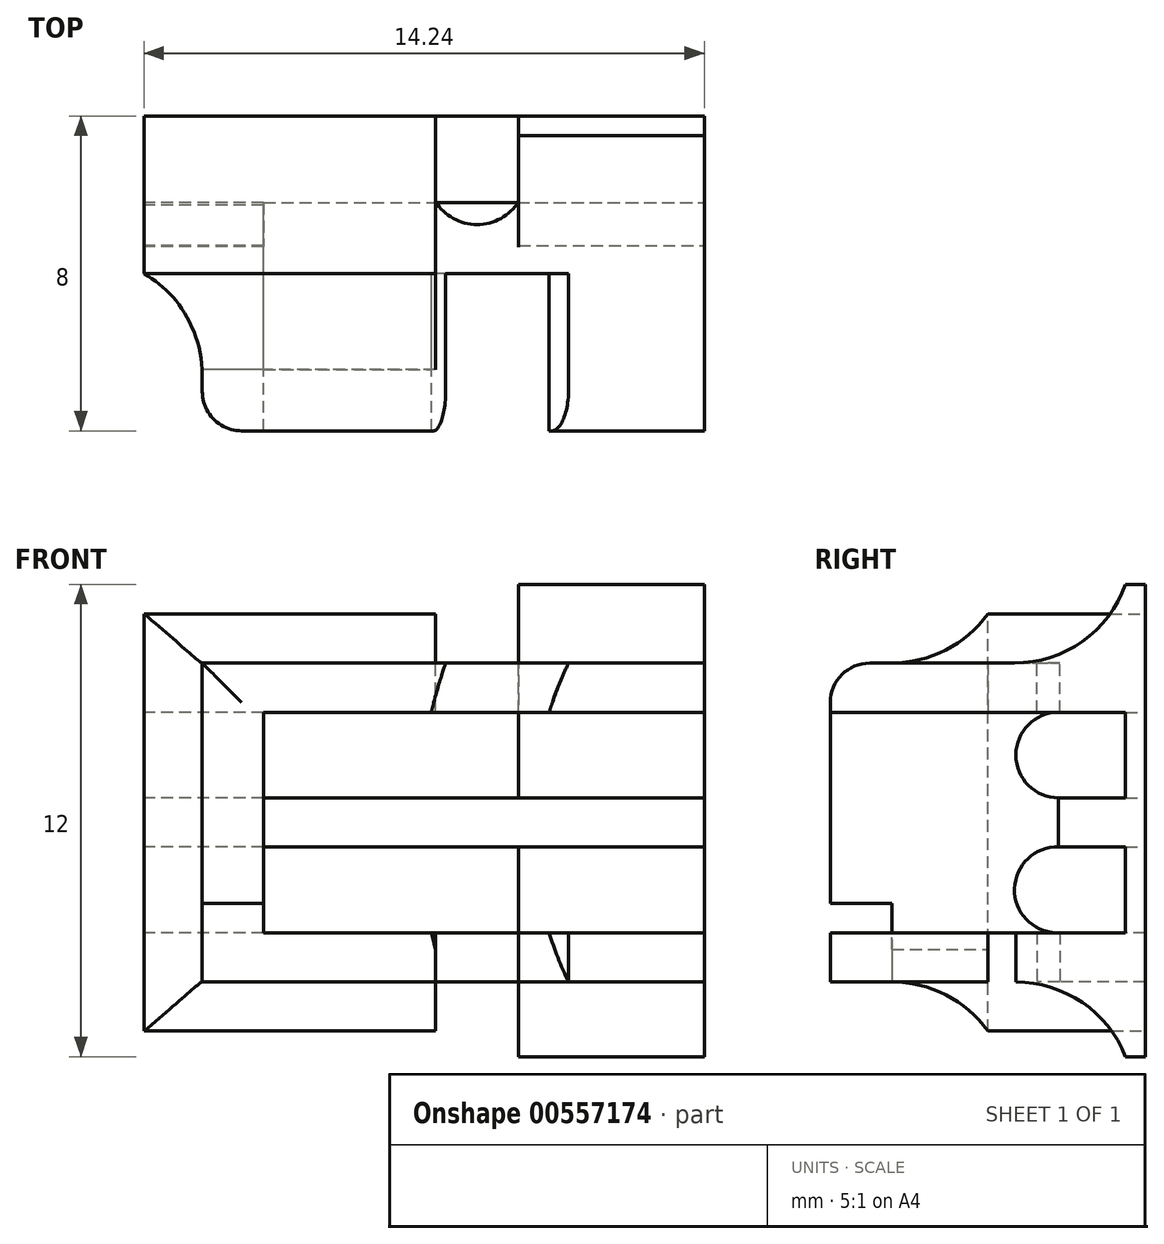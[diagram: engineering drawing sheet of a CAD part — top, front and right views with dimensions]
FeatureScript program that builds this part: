
annotation { "Feature Type Name" : "Feature", "Feature Type Description" : "" }
export const myFeature = defineFeature(function(context is Context, id is Id, definition is map)
    precondition{}
    {
        {
            var Q0;
            Q0=qCreatedBy(makeId("Front.planeOp"),FACE);
            var sketch = newSketch(context, id + "F0", { "sketchPlane" : qUnion([Q0])});
            skLineSegment(sketch, "E0.bottom", {"start": v(-5.6, 2.8) * mm, "end": v(-1.74, 2.8) * mm, "construction": true});
            skLineSegment(sketch, "E0.top", {"start": v(-5.6, -2.8) * mm, "end": v(-1.74, -2.8) * mm, "construction": true});
            skLineSegment(sketch, "E0.left", {"start": v(-5.6, 2.8) * mm, "end": v(-5.6, -2.8) * mm, "construction": true});
            skLineSegment(sketch, "E0.right", {"start": v(5.6, 2.8) * mm, "end": v(5.6, -2.8) * mm, "construction": true});
            skPoint(sketch, "E0.middle", {"position": v(0, 0) * mm});
            skLineSegment(sketch, "E1.bottom", {"start": v(-5.6, 0.62) * mm, "end": v(-1.23, 0.62) * mm});
            skLineSegment(sketch, "E1.top", {"start": v(-5.6, -0.62) * mm, "end": v(-1.23, -0.62) * mm});
            skLineSegment(sketch, "E1.left", {"start": v(-5.6, 0.62) * mm, "end": v(-5.6, -0.62) * mm});
            skLineSegment(sketch, "E1.right", {"start": v(5.6, 0.62) * mm, "end": v(5.6, -0.62) * mm});
            skLineSegment(sketch, "E2.bottom", {"start": v(-5.6, 4.05) * mm, "end": v(-1.23, 4.05) * mm});
            skLineSegment(sketch, "E2.top", {"start": v(-5.6, 2.8) * mm, "end": v(-1.74, 2.8) * mm});
            skLineSegment(sketch, "E2.left", {"start": v(-5.6, 4.05) * mm, "end": v(-5.6, 2.8) * mm});
            skLineSegment(sketch, "E2.right", {"start": v(5.6, 4.05) * mm, "end": v(5.6, 2.8) * mm});
            skLineSegment(sketch, "E3.bottom", {"start": v(5.6, -4.05) * mm, "end": v(0.88, -4.05) * mm});
            skLineSegment(sketch, "E3.top", {"start": v(5.6, -2.8) * mm, "end": v(1.23, -2.8) * mm});
            skLineSegment(sketch, "E3.left", {"start": v(5.6, -4.05) * mm, "end": v(5.6, -2.8) * mm});
            skLineSegment(sketch, "E3.right", {"start": v(-5.6, -4.05) * mm, "end": v(-5.6, -2.8) * mm});
            skLineSegment(sketch, "E4", {"start": v(1.23, 2.8) * mm, "end": v(1.23, 0.63) * mm, "construction": true});
            skLineSegment(sketch, "E5", {"start": v(-1.23, 2.8) * mm, "end": v(-1.23, 0.63) * mm, "construction": true});
            skLineSegment(sketch, "E6.bottom", {"start": v(-5.6, 4.05) * mm, "end": v(-7.16, 4.05) * mm});
            skLineSegment(sketch, "E6.top", {"start": v(-5.6, -4.05) * mm, "end": v(-7.16, -4.05) * mm});
            skLineSegment(sketch, "E6.left", {"start": v(-5.6, 4.05) * mm, "end": v(-5.6, -4.05) * mm});
            skLineSegment(sketch, "E6.right", {"start": v(-7.16, 4.05) * mm, "end": v(-7.16, -4.05) * mm});
            skLineSegment(sketch, "E7", {"start": v(-1.23, 4.05) * mm, "end": v(-1.23, 5.3) * mm});
            skLineSegment(sketch, "E8", {"start": v(-1.23, 5.3) * mm, "end": v(-8.64, 5.3) * mm});
            skLineSegment(sketch, "E9", {"start": v(-1.23, -4.05) * mm, "end": v(-1.23, -5.3) * mm});
            skLineSegment(sketch, "E10", {"start": v(-1.23, -5.3) * mm, "end": v(-8.64, -5.3) * mm});
            skLineSegment(sketch, "E11", {"start": v(-8.64, -5.3) * mm, "end": v(-8.64, 5.3) * mm});
            skLineSegment(sketch, "E12.trimOffspring", {"start": v(1.64, 0.62) * mm, "end": v(5.6, 0.62) * mm});
            skLineSegment(sketch, "E13.trimOffspring", {"start": v(1.64, -0.62) * mm, "end": v(5.6, -0.62) * mm});
            skLineSegment(sketch, "E14.trimOffspring", {"start": v(1.23, -2.8) * mm, "end": v(5.6, -2.8) * mm, "construction": true});
            skLineSegment(sketch, "E15.trimOffspring", {"start": v(-1.23, -4.05) * mm, "end": v(-5.6, -4.05) * mm});
            skLineSegment(sketch, "E16.trimOffspring", {"start": v(1.23, 2.8) * mm, "end": v(5.6, 2.8) * mm, "construction": true});
            skLineSegment(sketch, "E17.trimOffspring", {"start": v(1.23, 2.8) * mm, "end": v(5.6, 2.8) * mm});
            skLineSegment(sketch, "E18.trimOffspring", {"start": v(0.88, 4.05) * mm, "end": v(5.6, 4.05) * mm});
            skLineSegment(sketch, "E19.trimOffspring", {"start": v(-1.23, -2.8) * mm, "end": v(-5.6, -2.8) * mm});
            skLineSegment(sketch, "E20", {"start": v(-1.74, 2.8) * mm, "end": v(1.3, 2.8) * mm});
            skLineSegment(sketch, "E21", {"start": v(-2.33, 4.05) * mm, "end": v(0.88, 4.05) * mm});
            skLineSegment(sketch, "E22", {"start": v(-2.33, -4.05) * mm, "end": v(0.88, -4.05) * mm});
            skLineSegment(sketch, "E23", {"start": v(-1.74, -2.8) * mm, "end": v(1.23, -2.8) * mm});
            skLineSegment(sketch, "E24", {"start": v(-1.23, 0.62) * mm, "end": v(1.64, 0.62) * mm});
            skLineSegment(sketch, "E25", {"start": v(-1.23, -0.62) * mm, "end": v(1.64, -0.62) * mm});
            skLineSegment(sketch, "E26.trimOffspring", {"start": v(-1.23, -0.62) * mm, "end": v(-1.23, -2.8) * mm, "construction": true});
            skLineSegment(sketch, "E27.trimOffspring", {"start": v(1.23, -0.63) * mm, "end": v(1.23, -2.8) * mm, "construction": true});
            skArc(sketch, "E28", {"start": v(2.15, 4.05) * mm, "mid": v(1.88, 3.43) * mm, "end": v(1.66, 2.8) * mm});
            skArc(sketch, "E29.0", {"start": v(-0.97, 4.05) * mm, "mid": v(-1.17, 3.43) * mm, "end": v(-1.34, 2.8) * mm});
            skArc(sketch, "E30.trimOffspring", {"start": v(-1.64, 0.63) * mm, "mid": v(-1.66, 0) * mm, "end": v(-1.64, -0.62) * mm});
            skArc(sketch, "E31.trimOffspring", {"start": v(-1.34, -2.8) * mm, "mid": v(-1.17, -3.43) * mm, "end": v(-0.97, -4.05) * mm});
            skArc(sketch, "E32.trimOffspring", {"start": v(1.25, 0.62) * mm, "mid": v(1.23, 0) * mm, "end": v(1.25, -0.63) * mm});
            skArc(sketch, "E33.trimOffspring", {"start": v(1.66, -2.8) * mm, "mid": v(1.88, -3.43) * mm, "end": v(2.15, -4.05) * mm});
            skSolve(sketch);
        }
        {
            var Q0;
            {var subQ0=sQuery(id+"F0.wireOp",EDGE,"E1.bottom");Q0=makeQuery(id+"F0.imprint","IMPRINT",FACE,{"disambiguationData":[TD([[makeQuery(id+"F0.imprint","IMPRINT",EDGE,{"derivedFrom":subQ0}),-1.0]])]});}
            var Q1;
            {var subQ7=sQuery(id+"F0.wireOp",EDGE,"E30.trimOffspring");Q1=makeQuery(id+"F0.imprint","IMPRINT",FACE,{"disambiguationData":[TD([[makeQuery(id+"F0.imprint","IMPRINT",EDGE,{"derivedFrom":subQ7}),1.0]])]});}
            var Q2;
            Q2=makeQuery(id+"F0.imprint","IMPRINT",FACE,{"disambiguationData":[TD([[makeQuery(id+"F0.imprint","IMPRINT",EDGE,{"derivedFrom":sQuery(id+"F0.wireOp",EDGE,"E1.right")}),-1.0]])]});
            extrude(context, id + "F1", {"entities" : qUnion([Q0, Q1, Q2]), "depth" : 2.2 * mm, "offsetDistance" : 25 * mm});
        }
        {
            var Q0;
            {var subQ0=sQuery(id+"F0.wireOp",EDGE,"E3.left");Q0=makeQuery(id+"F0.imprint","IMPRINT",FACE,{"disambiguationData":[TD([[makeQuery(id+"F0.imprint","IMPRINT",EDGE,{"derivedFrom":subQ0}),1.0]])]});}
            var Q1;
            {var subQ3=sQuery(id+"F0.wireOp",EDGE,"E31.trimOffspring");Q1=makeQuery(id+"F0.imprint","IMPRINT",FACE,{"disambiguationData":[TD([[makeQuery(id+"F0.imprint","IMPRINT",EDGE,{"derivedFrom":subQ3}),1.0]])]});}
            var Q2;
            {var subQ1=sQuery(id+"F0.wireOp",EDGE,"E15.trimOffspring");Q2=makeQuery(id+"F0.imprint","IMPRINT",FACE,{"disambiguationData":[TD([[makeQuery(id+"F0.imprint","IMPRINT",EDGE,{"derivedFrom":subQ1}),-1.0]])]});}
            var Q3;
            {var subQ1=sQuery(id+"F0.wireOp",EDGE,"E2.bottom");Q3=makeQuery(id+"F0.imprint","IMPRINT",FACE,{"disambiguationData":[TD([[makeQuery(id+"F0.imprint","IMPRINT",EDGE,{"derivedFrom":subQ1}),1.0]])]});}
            var Q4;
            {var subQ3=sQuery(id+"F0.wireOp",EDGE,"E6.bottom");Q4=makeQuery(id+"F0.imprint","IMPRINT",FACE,{"disambiguationData":[TD([[makeQuery(id+"F0.imprint","IMPRINT",EDGE,{"derivedFrom":subQ3}),1.0]])]});}
            var Q5;
            {var subQ4=sQuery(id+"F0.wireOp",EDGE,"E2.bottom");Q5=makeQuery(id+"F0.imprint","IMPRINT",FACE,{"disambiguationData":[TD([[makeQuery(id+"F0.imprint","IMPRINT",EDGE,{"derivedFrom":subQ4}),-1.0]])]});}
            var Q6;
            {var subQ7=sQuery(id+"F0.wireOp",EDGE,"E28");Q6=makeQuery(id+"F0.imprint","IMPRINT",FACE,{"disambiguationData":[TD([[makeQuery(id+"F0.imprint","IMPRINT",EDGE,{"derivedFrom":subQ7}),-1.0]])]});}
            var Q7;
            {var subQ0=sQuery(id+"F0.wireOp",EDGE,"E2.right");Q7=makeQuery(id+"F0.imprint","IMPRINT",FACE,{"disambiguationData":[TD([[makeQuery(id+"F0.imprint","IMPRINT",EDGE,{"derivedFrom":subQ0}),-1.0]])]});}
            extrude(context, id + "F2", {"entities" : qUnion([Q0, Q1, Q2, Q3, Q4, Q5, Q6, Q7]), "operationType" : NewBodyOperationType.ADD, "depth" : 4 * mm, "offsetDistance" : 25 * mm});
        }
        {
            var Q0;
            {var subQ0=sQuery(id+"F0.wireOp",EDGE,"E2.right");Q0=makeQuery(id+"F0.imprint","IMPRINT",FACE,{"disambiguationData":[TD([[makeQuery(id+"F0.imprint","IMPRINT",EDGE,{"derivedFrom":subQ0}),-1.0]])]});}
            var Q1;
            {var subQ4=sQuery(id+"F0.wireOp",EDGE,"E2.bottom");Q1=makeQuery(id+"F0.imprint","IMPRINT",FACE,{"disambiguationData":[TD([[makeQuery(id+"F0.imprint","IMPRINT",EDGE,{"derivedFrom":subQ4}),-1.0]])]});}
            var Q2;
            {var subQ3=sQuery(id+"F0.wireOp",EDGE,"E6.bottom");Q2=makeQuery(id+"F0.imprint","IMPRINT",FACE,{"disambiguationData":[TD([[makeQuery(id+"F0.imprint","IMPRINT",EDGE,{"derivedFrom":subQ3}),1.0]])]});}
            var Q3;
            {var subQ1=sQuery(id+"F0.wireOp",EDGE,"E15.trimOffspring");Q3=makeQuery(id+"F0.imprint","IMPRINT",FACE,{"disambiguationData":[TD([[makeQuery(id+"F0.imprint","IMPRINT",EDGE,{"derivedFrom":subQ1}),-1.0]])]});}
            var Q4;
            {var subQ0=sQuery(id+"F0.wireOp",EDGE,"E3.left");Q4=makeQuery(id+"F0.imprint","IMPRINT",FACE,{"disambiguationData":[TD([[makeQuery(id+"F0.imprint","IMPRINT",EDGE,{"derivedFrom":subQ0}),1.0]])]});}
            extrude(context, id + "F3", {"entities" : qUnion([Q0, Q1, Q2, Q3, Q4]), "operationType" : NewBodyOperationType.ADD, "depth" : 8 * mm, "offsetDistance" : 25 * mm});
        }
        {
            var Q0;
            Q0=makeQuery(id+"F2.opExtrude","SWEPT_FACE",FACE,{"disambiguationData":[OSD([sQuery(id+"F0.wireOp",EDGE,"E11")])]});
            var sketch = newSketch(context, id + "F4", { "sketchPlane" : qUnion([Q0])});
            skLineSegment(sketch, "E34.0", {"start": v(8, 2.8) * mm, "end": v(0, 2.8) * mm});
            skLineSegment(sketch, "E34.1", {"start": v(2.2, 0.62) * mm, "end": v(0, 0.62) * mm});
            skLineSegment(sketch, "E34.2", {"start": v(2.2, 0.62) * mm, "end": v(2.2, -0.62) * mm});
            skLineSegment(sketch, "E34.3", {"start": v(2.2, -0.62) * mm, "end": v(0, -0.62) * mm});
            skLineSegment(sketch, "E34.4", {"start": v(8, -2.8) * mm, "end": v(0, -2.8) * mm});
            skLineSegment(sketch, "E35", {"start": v(2.2, 2.8) * mm, "end": v(2.2, -2.8) * mm, "construction": true});
            skArc(sketch, "E36", {"start": v(2.2, 0.62) * mm, "mid": v(3.29, 1.71) * mm, "end": v(2.2, 2.8) * mm});
            skArc(sketch, "E37", {"start": v(2.2, -2.8) * mm, "mid": v(3.32, -1.71) * mm, "end": v(2.2, -0.63) * mm});
            skSolve(sketch);
        }
        {
            var Q0;
            {var subQ0=sQuery(id+"F0.wireOp",EDGE,"E18.trimOffspring");Q0=makeQuery(id+"F3.boolean.opBoolean","MERGE",FACE,{"derivedFrom":[makeQuery(id+"F2.opExtrude","SWEPT_FACE",FACE,{"disambiguationData":[OSD([subQ0,sQuery(id+"F0.wireOp",EDGE,"E21")])]}),makeQuery(id+"F3.opExtrude","SWEPT_FACE",FACE,{"disambiguationData":[OSD([subQ0])]})]});}
            var sketch = newSketch(context, id + "F5", { "sketchPlane" : qUnion([Q0])});
            skLineSegment(sketch, "E38.bottom", {"start": v(5.6, 0) * mm, "end": v(0.88, 0) * mm});
            skLineSegment(sketch, "E38.top", {"start": v(5.6, -0.5) * mm, "end": v(0.88, -0.5) * mm});
            skLineSegment(sketch, "E38.left", {"start": v(5.6, 0) * mm, "end": v(5.6, -0.5) * mm});
            skLineSegment(sketch, "E38.right", {"start": v(0.88, 0) * mm, "end": v(0.88, -0.5) * mm});
            skSolve(sketch);
        }
        {
            var Q0;
            Q0=makeQuery(id+"F5.imprint","IMPRINT",FACE,{"disambiguationData":[TD([[makeQuery(id+"F5.imprint","IMPRINT",EDGE,{"derivedFrom":sQuery(id+"F5.wireOp",EDGE,"E38.bottom")}),-1.0]])]});
            extrude(context, id + "F6", {"entities" : qUnion([Q0]), "operationType" : NewBodyOperationType.ADD, "depth" : 2 * mm, "offsetDistance" : 25 * mm, "hasSecondDirection" : true, "secondDirectionOppositeDirection" : true, "secondDirectionDepth" : 10 * mm});
        }
        {
            var Q0;
            {var subQ4=sQuery(id+"F4.wireOp",EDGE,"E34.1");Q0=makeQuery(id+"F4.imprint","IMPRINT",FACE,{"disambiguationData":[TD([[makeQuery(id+"F4.imprint","IMPRINT",EDGE,{"derivedFrom":subQ4}),-1.0]])]});}
            var Q1;
            {var subQ1=sQuery(id+"F4.wireOp",EDGE,"E34.3");Q1=makeQuery(id+"F4.imprint","IMPRINT",FACE,{"disambiguationData":[TD([[makeQuery(id+"F4.imprint","IMPRINT",EDGE,{"derivedFrom":subQ1}),1.0]])]});}
            extrude(context, id + "F7", {"entities" : qUnion([Q0, Q1]), "operationType" : NewBodyOperationType.REMOVE, "oppositeDirection" : true, "depth" : 4 * mm, "offsetDistance" : 25 * mm});
        }
        {
            var Q0;
            {var subQ0=sQuery(id+"F0.wireOp",EDGE,"E21");Q0=makeQuery(id+"F3.boolean.opBoolean","INTERSECT",EDGE,{"derivedFrom":[makeQuery(id+"F2.opExtrude","CAP_FACE",FACE,{"disambiguationData":[OSD([sQuery(id+"F0.wireOp",EDGE,"E2.top"),sQuery(id+"F0.wireOp",EDGE,"E2.right"),sQuery(id+"F0.wireOp",EDGE,"E3.bottom"),sQuery(id+"F0.wireOp",EDGE,"E3.top"),sQuery(id+"F0.wireOp",EDGE,"E3.left"),sQuery(id+"F0.wireOp",EDGE,"E6.left"),sQuery(id+"F0.wireOp",EDGE,"E7"),sQuery(id+"F0.wireOp",EDGE,"E8"),sQuery(id+"F0.wireOp",EDGE,"E9"),sQuery(id+"F0.wireOp",EDGE,"E10"),sQuery(id+"F0.wireOp",EDGE,"E11"),sQuery(id+"F0.wireOp",EDGE,"E17.trimOffspring"),sQuery(id+"F0.wireOp",EDGE,"E18.trimOffspring"),sQuery(id+"F0.wireOp",EDGE,"E19.trimOffspring"),sQuery(id+"F0.wireOp",EDGE,"E20"),subQ0,sQuery(id+"F0.wireOp",EDGE,"E22"),sQuery(id+"F0.wireOp",EDGE,"E23")])],"isStart":false}),makeQuery(id+"F3.opExtrude","SWEPT_FACE",FACE,{"disambiguationData":[OSD([sQuery(id+"F0.wireOp",EDGE,"E2.bottom"),sQuery(id+"F0.wireOp",EDGE,"E6.bottom"),subQ0])]})]});}
            var Q1;
            Q1=makeQuery(id+"F3.boolean.opBoolean","INTERSECT",EDGE,{"derivedFrom":[makeQuery(id+"F2.opExtrude","CAP_FACE",FACE,{"disambiguationData":[OSD([sQuery(id+"F0.wireOp",EDGE,"E2.top"),sQuery(id+"F0.wireOp",EDGE,"E2.right"),sQuery(id+"F0.wireOp",EDGE,"E3.bottom"),sQuery(id+"F0.wireOp",EDGE,"E3.top"),sQuery(id+"F0.wireOp",EDGE,"E3.left"),sQuery(id+"F0.wireOp",EDGE,"E6.left"),sQuery(id+"F0.wireOp",EDGE,"E7"),sQuery(id+"F0.wireOp",EDGE,"E8"),sQuery(id+"F0.wireOp",EDGE,"E9"),sQuery(id+"F0.wireOp",EDGE,"E10"),sQuery(id+"F0.wireOp",EDGE,"E11"),sQuery(id+"F0.wireOp",EDGE,"E17.trimOffspring"),sQuery(id+"F0.wireOp",EDGE,"E18.trimOffspring"),sQuery(id+"F0.wireOp",EDGE,"E19.trimOffspring"),sQuery(id+"F0.wireOp",EDGE,"E20"),sQuery(id+"F0.wireOp",EDGE,"E21"),sQuery(id+"F0.wireOp",EDGE,"E22"),sQuery(id+"F0.wireOp",EDGE,"E23")])],"isStart":false}),makeQuery(id+"F3.opExtrude","SWEPT_FACE",FACE,{"disambiguationData":[OSD([sQuery(id+"F0.wireOp",EDGE,"E6.right")])]})]});
            var Q2;
            {var subQ0=sQuery(id+"F0.wireOp",EDGE,"E22");Q2=makeQuery(id+"F3.boolean.opBoolean","INTERSECT",EDGE,{"derivedFrom":[makeQuery(id+"F2.opExtrude","CAP_FACE",FACE,{"disambiguationData":[OSD([sQuery(id+"F0.wireOp",EDGE,"E2.top"),sQuery(id+"F0.wireOp",EDGE,"E2.right"),sQuery(id+"F0.wireOp",EDGE,"E3.bottom"),sQuery(id+"F0.wireOp",EDGE,"E3.top"),sQuery(id+"F0.wireOp",EDGE,"E3.left"),sQuery(id+"F0.wireOp",EDGE,"E6.left"),sQuery(id+"F0.wireOp",EDGE,"E7"),sQuery(id+"F0.wireOp",EDGE,"E8"),sQuery(id+"F0.wireOp",EDGE,"E9"),sQuery(id+"F0.wireOp",EDGE,"E10"),sQuery(id+"F0.wireOp",EDGE,"E11"),sQuery(id+"F0.wireOp",EDGE,"E17.trimOffspring"),sQuery(id+"F0.wireOp",EDGE,"E18.trimOffspring"),sQuery(id+"F0.wireOp",EDGE,"E19.trimOffspring"),sQuery(id+"F0.wireOp",EDGE,"E20"),sQuery(id+"F0.wireOp",EDGE,"E21"),subQ0,sQuery(id+"F0.wireOp",EDGE,"E23")])],"isStart":false}),makeQuery(id+"F3.opExtrude","SWEPT_FACE",FACE,{"disambiguationData":[OSD([sQuery(id+"F0.wireOp",EDGE,"E6.top"),sQuery(id+"F0.wireOp",EDGE,"E15.trimOffspring"),subQ0])]})]});}
            var Q3;
            {var subQ0=sQuery(id+"F0.wireOp",EDGE,"E22");var subQ1=sQuery(id+"F0.wireOp",EDGE,"E3.bottom");Q3=makeQuery(id+"F6.boolean.opBoolean","INTERSECT",EDGE,{"derivedFrom":[makeQuery(id+"F3.boolean.opBoolean","MERGE",FACE,{"derivedFrom":[makeQuery(id+"F2.opExtrude","SWEPT_FACE",FACE,{"disambiguationData":[OSD([subQ1,subQ0])]}),makeQuery(id+"F3.opExtrude","SWEPT_FACE",FACE,{"disambiguationData":[OSD([subQ1])]}),makeQuery(id+"F3.opExtrude","SWEPT_FACE",FACE,{"disambiguationData":[OSD([sQuery(id+"F0.wireOp",EDGE,"E6.top"),sQuery(id+"F0.wireOp",EDGE,"E15.trimOffspring"),subQ0])]})]}),makeQuery(id+"F6.opExtrude","SWEPT_FACE",FACE,{"disambiguationData":[OSD([sQuery(id+"F5.wireOp",EDGE,"E38.top")])]})]});}
            var Q4;
            {var subQ0=sQuery(id+"F0.wireOp",EDGE,"E18.trimOffspring");var subQ1=sQuery(id+"F0.wireOp",EDGE,"E21");Q4=makeQuery(id+"F6.boolean.opBoolean","INTERSECT",EDGE,{"derivedFrom":[makeQuery(id+"F3.boolean.opBoolean","MERGE",FACE,{"derivedFrom":[makeQuery(id+"F2.opExtrude","SWEPT_FACE",FACE,{"disambiguationData":[OSD([subQ0,subQ1])]}),makeQuery(id+"F3.opExtrude","SWEPT_FACE",FACE,{"disambiguationData":[OSD([sQuery(id+"F0.wireOp",EDGE,"E2.bottom"),sQuery(id+"F0.wireOp",EDGE,"E6.bottom"),subQ1])]}),makeQuery(id+"F3.opExtrude","SWEPT_FACE",FACE,{"disambiguationData":[OSD([subQ0])]})]}),makeQuery(id+"F6.opExtrude","SWEPT_FACE",FACE,{"disambiguationData":[OSD([sQuery(id+"F5.wireOp",EDGE,"E38.top")])]})]});}
            fillet(context, id + "F8", {"entities" : qUnion([Q0, Q1, Q2, Q3, Q4]), "radius" : 3 * mm, "tangentPropagation" : true, "allowEdgeOverflow" : false});
        }
        {
            var Q0;
            {var subQ0=sQuery(id+"F0.wireOp",EDGE,"E18.trimOffspring");var subQ1=sQuery(id+"F0.wireOp",EDGE,"E21");Q0=makeQuery(id+"F3.boolean.opBoolean","MERGE",FACE,{"derivedFrom":[makeQuery(id+"F2.opExtrude","SWEPT_FACE",FACE,{"disambiguationData":[OSD([subQ0,subQ1])]}),makeQuery(id+"F3.opExtrude","SWEPT_FACE",FACE,{"disambiguationData":[OSD([sQuery(id+"F0.wireOp",EDGE,"E2.bottom"),sQuery(id+"F0.wireOp",EDGE,"E6.bottom"),subQ1])]}),makeQuery(id+"F3.opExtrude","SWEPT_FACE",FACE,{"disambiguationData":[OSD([subQ0])]})]});}
            var sketch = newSketch(context, id + "F9", { "sketchPlane" : qUnion([Q0])});
            skLineSegment(sketch, "E39", {"start": v(0.88, -2.17) * mm, "end": v(-1.23, -2.17) * mm, "construction": true});
            skArc(sketch, "E40", {"start": v(-1.23, -2.17) * mm, "mid": v(-0.18, -2.76) * mm, "end": v(0.88, -2.17) * mm});
            skSolve(sketch);
        }
        {
            var Q0;
            {var subQ0=sQuery(id+"F9.wireOp",EDGE,"E40");Q0=makeQuery(id+"F9.imprint","IMPRINT",FACE,{"disambiguationData":[TD([[makeQuery(id+"F9.imprint","IMPRINT",EDGE,{"derivedFrom":subQ0}),1.0]])]});}
            extrude(context, id + "F10", {"entities" : qUnion([Q0]), "operationType" : NewBodyOperationType.REMOVE, "oppositeDirection" : true, "depth" : 1.5 * mm, "offsetDistance" : 25 * mm});
        }
        {
            var Q0;
            {var subQ0=sQuery(id+"F0.wireOp",EDGE,"E22");var subQ1=sQuery(id+"F0.wireOp",EDGE,"E3.bottom");Q0=makeQuery(id+"F3.boolean.opBoolean","MERGE",FACE,{"derivedFrom":[makeQuery(id+"F2.opExtrude","SWEPT_FACE",FACE,{"disambiguationData":[OSD([subQ1,subQ0])]}),makeQuery(id+"F3.opExtrude","SWEPT_FACE",FACE,{"disambiguationData":[OSD([subQ1])]}),makeQuery(id+"F3.opExtrude","SWEPT_FACE",FACE,{"disambiguationData":[OSD([sQuery(id+"F0.wireOp",EDGE,"E6.top"),sQuery(id+"F0.wireOp",EDGE,"E15.trimOffspring"),subQ0])]})]});}
            var sketch = newSketch(context, id + "F11", { "sketchPlane" : qUnion([Q0])});
            skArc(sketch, "E41.0", {"start": v(-1.23, 2.17) * mm, "mid": v(-0.18, 2.76) * mm, "end": v(0.88, 2.17) * mm});
            skLineSegment(sketch, "E41.1", {"start": v(0.88, 0.5) * mm, "end": v(0.88, 3.3) * mm});
            skLineSegment(sketch, "E41.2", {"start": v(0.88, 0) * mm, "end": v(0.88, 0.5) * mm});
            skLineSegment(sketch, "E41.3", {"start": v(-1.23, 4) * mm, "end": v(-1.23, 0) * mm});
            skSolve(sketch);
        }
        {
            var Q0;
            {var subQ2=sQuery(id+"F11.wireOp",EDGE,"E41.0");Q0=makeQuery(id+"F11.imprint","IMPRINT",FACE,{"disambiguationData":[TD([[makeQuery(id+"F11.imprint","IMPRINT",EDGE,{"derivedFrom":subQ2}),-1.0]])]});}
            extrude(context, id + "F12", {"entities" : qUnion([Q0]), "operationType" : NewBodyOperationType.REMOVE, "oppositeDirection" : true, "depth" : 2 * mm, "offsetDistance" : 25 * mm});
        }
        {
            var Q0;
            Q0=makeQuery(id+"F3.opExtrude","CAP_EDGE",EDGE,{"disambiguationData":[OSD([sQuery(id+"F0.wireOp",EDGE,"E2.bottom"),sQuery(id+"F0.wireOp",EDGE,"E6.bottom"),sQuery(id+"F0.wireOp",EDGE,"E21")])],"isStart":false});
            var Q1;
            Q1=makeQuery(id+"F3.opExtrude","CAP_EDGE",EDGE,{"disambiguationData":[OSD([sQuery(id+"F0.wireOp",EDGE,"E6.right")])],"isStart":false});
            var Q2;
            Q2=makeQuery(id+"F3.opExtrude","CAP_EDGE",EDGE,{"disambiguationData":[OSD([sQuery(id+"F0.wireOp",EDGE,"E6.top"),sQuery(id+"F0.wireOp",EDGE,"E15.trimOffspring"),sQuery(id+"F0.wireOp",EDGE,"E22")])],"isStart":false});
            var Q3;
            Q3=makeQuery(id+"F3.opExtrude","CAP_EDGE",EDGE,{"disambiguationData":[OSD([sQuery(id+"F0.wireOp",EDGE,"E3.bottom")])],"isStart":false});
            var Q4;
            Q4=makeQuery(id+"F3.opExtrude","CAP_EDGE",EDGE,{"disambiguationData":[OSD([sQuery(id+"F0.wireOp",EDGE,"E18.trimOffspring")])],"isStart":false});
            fillet(context, id + "F13", {"entities" : qUnion([Q0, Q1, Q2, Q3, Q4]), "radius" : 1 * mm, "tangentPropagation" : true, "allowEdgeOverflow" : false});
        }
    });
